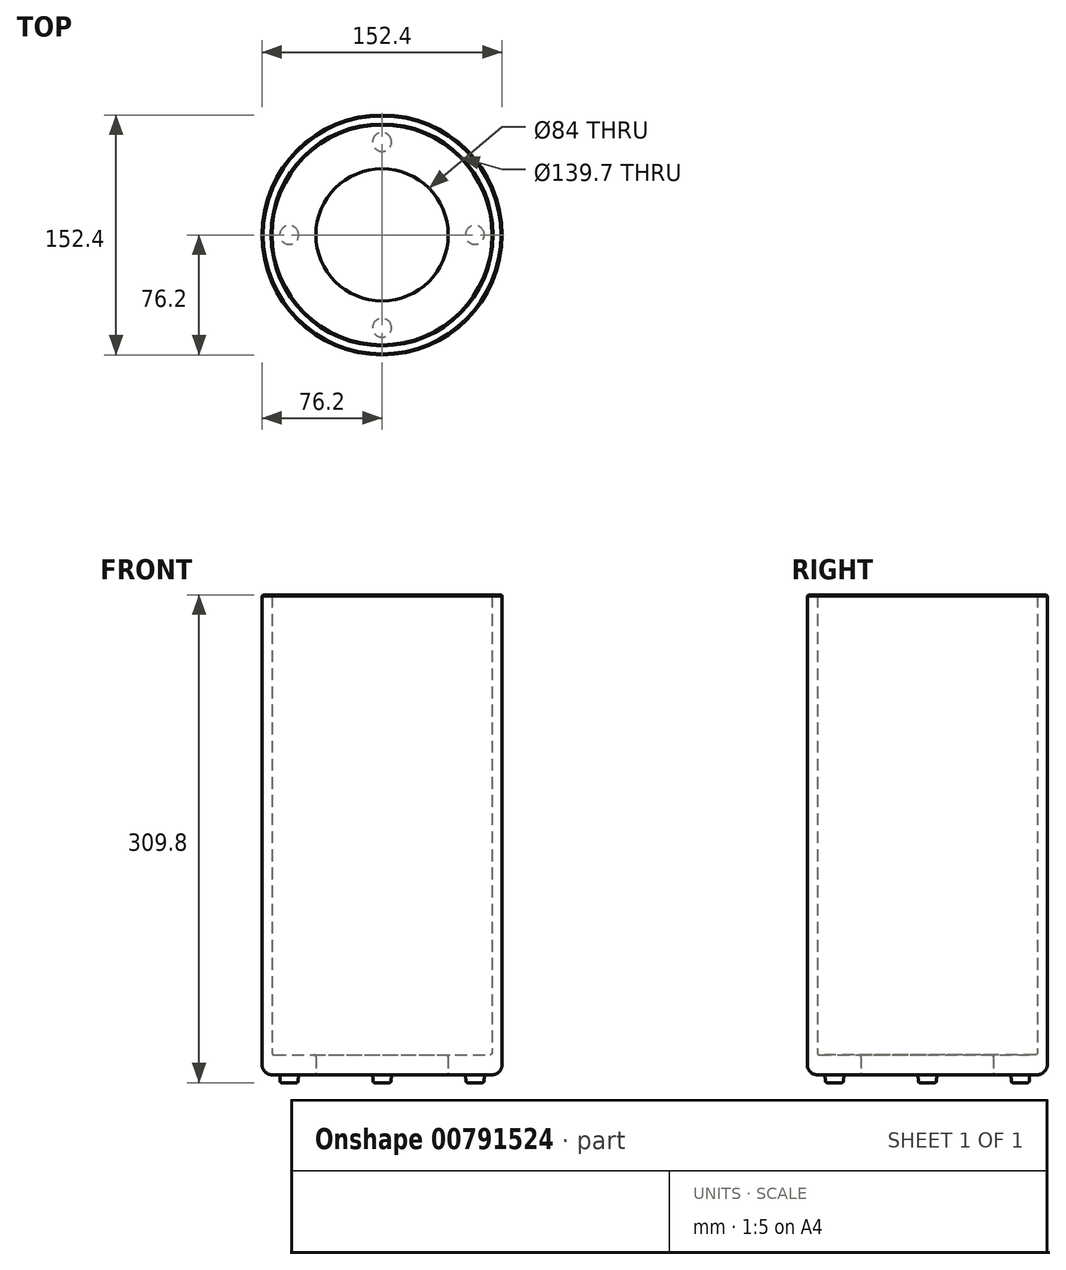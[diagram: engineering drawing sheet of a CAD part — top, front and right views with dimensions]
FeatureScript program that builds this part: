
annotation { "Feature Type Name" : "Feature", "Feature Type Description" : "" }
export const myFeature = defineFeature(function(context is Context, id is Id, definition is map)
    precondition{}
    {
        {
            var Q0;
            Q0=qCreatedBy(makeId("Front.planeOp"),FACE);
            var sketch = newSketch(context, id + "F0", { "sketchPlane" : qUnion([Q0])});
            skLineSegment(sketch, "E0", {"start": v(-43.27, 0) * mm, "end": v(-69.85, 0) * mm});
            skLineSegment(sketch, "E1", {"start": v(-76.2, 6.35) * mm, "end": v(-76.2, 304.8) * mm});
            skLineSegment(sketch, "E2", {"start": v(-76.2, 304.8) * mm, "end": v(-69.85, 304.8) * mm});
            skLineSegment(sketch, "E3", {"start": v(-69.85, 304.8) * mm, "end": v(-69.85, 13.97) * mm});
            skLineSegment(sketch, "E4", {"start": v(-68.58, 12.7) * mm, "end": v(-43.27, 12.7) * mm});
            skLineSegment(sketch, "E5", {"start": v(-42, 11.43) * mm, "end": v(-42, 1.27) * mm});
            skPoint(sketch, "E6.visualSharp", {"position": v(-42, 12.7) * mm});
            skArc(sketch, "E6.filletArc", {"start": v(-42, 11.43) * mm, "mid": v(-42.37, 12.33) * mm, "end": v(-43.27, 12.7) * mm});
            skPoint(sketch, "E7.visualSharp", {"position": v(-42, 0) * mm});
            skArc(sketch, "E7.filletArc", {"start": v(-43.27, 0) * mm, "mid": v(-42.37, 0.37) * mm, "end": v(-42, 1.27) * mm});
            skPoint(sketch, "E8.visualSharp", {"position": v(-76.2, 0) * mm});
            skArc(sketch, "E8.filletArc", {"start": v(-76.2, 6.35) * mm, "mid": v(-74.34, 1.86) * mm, "end": v(-69.85, 0) * mm});
            skPoint(sketch, "E9.visualSharp", {"position": v(-69.85, 12.7) * mm});
            skArc(sketch, "E9.filletArc", {"start": v(-69.85, 13.97) * mm, "mid": v(-69.48, 13.07) * mm, "end": v(-68.58, 12.7) * mm});
            skSolve(sketch);
        }
        {
            var Q0;
            Q0=qCreatedBy(makeId("Front.planeOp"),FACE);
            var sketch = newSketch(context, id + "F1", { "sketchPlane" : qUnion([Q0])});
            skLineSegment(sketch, "E10", {"start": v(0, 0) * mm, "end": v(0, 88.55) * mm, "construction": true});
            skSolve(sketch);
        }
        {
            var Q0;
            Q0 = qSketchRegion(id + "F0", true);
            var Q1;
            Q1=sQuery(id+"F1.wireOp",EDGE,"E10");
            revolve(context, id + "F2", {"surfaceOperationType" : NewSurfaceOperationType.NEW, "entities" : qUnion([Q0]), "axis" : qUnion([Q1]), "revolveType" : RevolveType.FULL});
        }
        {
            var Q0;
            Q0=makeQuery(id+"F2.opRevolve","SWEPT_EDGE",EDGE,{"disambiguationData":[OSD([sQuery(id+"F0.wireOp",EDGE,"E2"),sQuery(id+"F0.wireOp",EDGE,"E3")])]});
            var Q1;
            Q1=makeQuery(id+"F2.opRevolve","SWEPT_EDGE",EDGE,{"disambiguationData":[OSD([sQuery(id+"F0.wireOp",EDGE,"E1"),sQuery(id+"F0.wireOp",EDGE,"E2")])]});
            chamfer(context, id + "F3", {"entities" : qUnion([Q0, Q1]), "width" : 0.64 * mm, "tangentPropagation" : true});
        }
        {
            var Q0;
            Q0=makeQuery(id+"F2.opRevolve","SWEPT_FACE",FACE,{"disambiguationData":[OSD([sQuery(id+"F0.wireOp",EDGE,"E0")])]});
            var sketch = newSketch(context, id + "F4", { "sketchPlane" : qUnion([Q0])});
            skCircle(sketch, "E11", {"center": v(0, 59) * mm, "radius": 6 * mm});
            skCircle(sketch, "E12.1.0", {"center": v(-59, 0) * mm, "radius": 6 * mm});
            skCircle(sketch, "E12.2.0", {"center": v(0, -59) * mm, "radius": 6 * mm});
            skCircle(sketch, "E12.3.0", {"center": v(59, 0) * mm, "radius": 6 * mm});
            skPoint(sketch, "E12.center", {"position": v(0, 0) * mm});
            skSolve(sketch);
        }
        {
            var Q0;
            Q0 = qSketchRegion(id + "F4", true);
            extrude(context, id + "F5", {"entities" : qUnion([Q0]), "operationType" : NewBodyOperationType.ADD, "depth" : 5 * mm, "offsetDistance" : 25 * mm, "hasDraft" : true, "draftAngle" : 4 * degree, "draftPullDirection" : true});
        }
        {
            var Q0;
            Q0=makeQuery(id+"F5.opExtrude","CAP_FACE",FACE,{"disambiguationData":[OSD([sQuery(id+"F4.wireOp",EDGE,"E11")])],"isStart":false});
            var Q1;
            Q1=makeQuery(id+"F5.opExtrude","CAP_FACE",FACE,{"disambiguationData":[OSD([sQuery(id+"F4.wireOp",EDGE,"E12.1.0")])],"isStart":false});
            var Q2;
            Q2=makeQuery(id+"F5.opExtrude","CAP_FACE",FACE,{"disambiguationData":[OSD([sQuery(id+"F4.wireOp",EDGE,"E12.2.0")])],"isStart":false});
            var Q3;
            Q3=makeQuery(id+"F5.opExtrude","CAP_FACE",FACE,{"disambiguationData":[OSD([sQuery(id+"F4.wireOp",EDGE,"E12.3.0")])],"isStart":false});
            fillet(context, id + "F6", {"entities" : qUnion([Q0, Q1, Q2, Q3]), "radius" : 1 * mm, "tangentPropagation" : true, "allowEdgeOverflow" : false});
        }
    });
